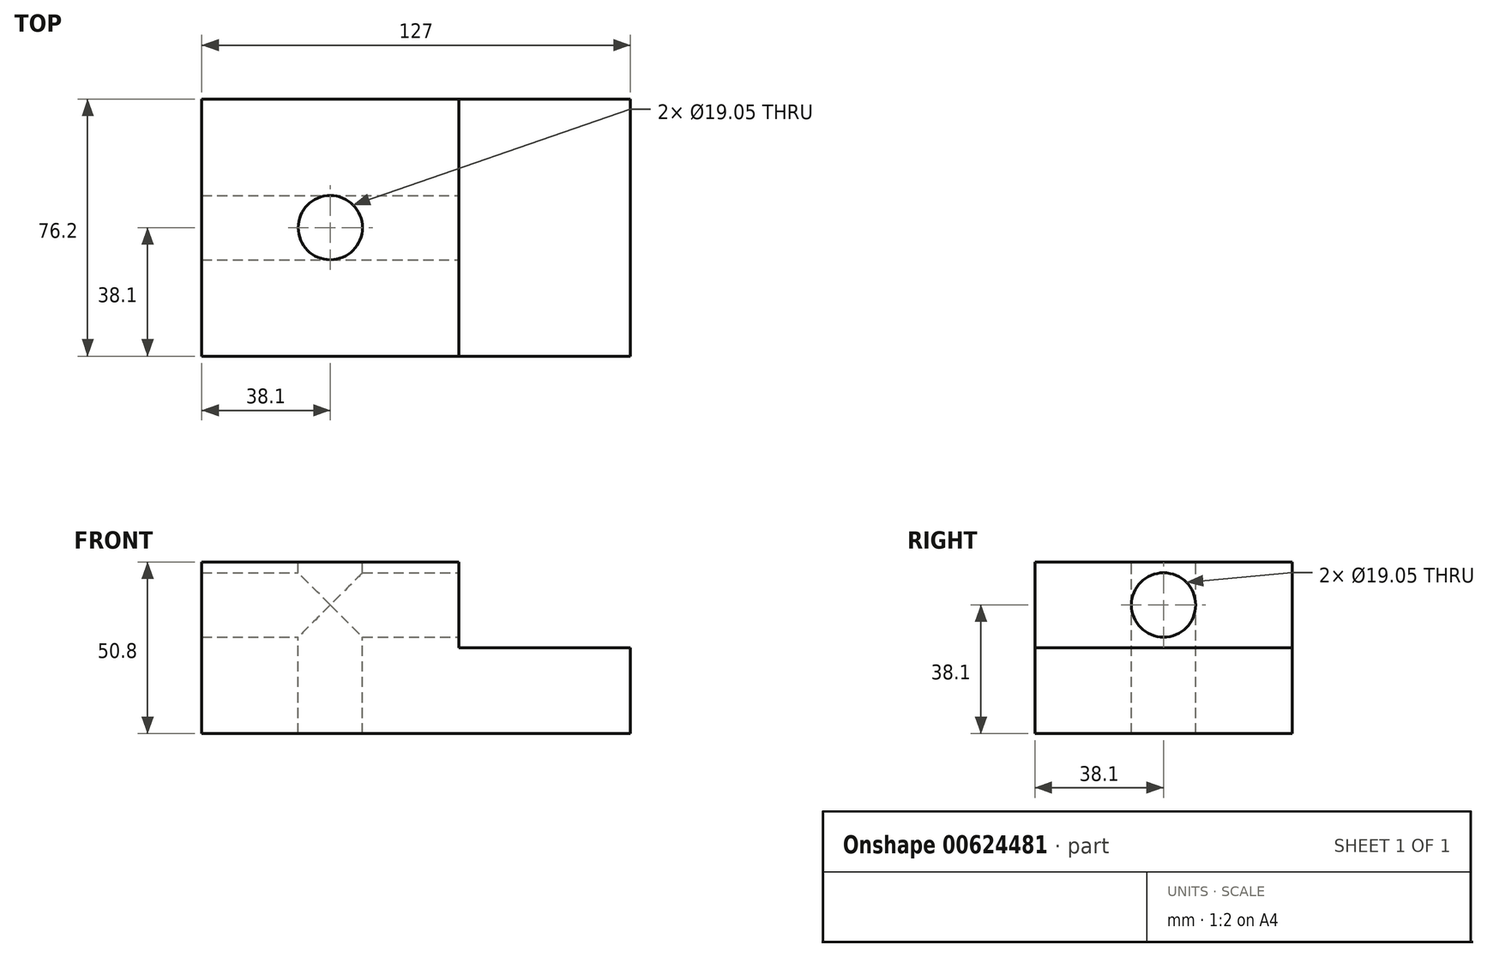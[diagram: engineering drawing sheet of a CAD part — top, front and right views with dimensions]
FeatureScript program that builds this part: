
annotation { "Feature Type Name" : "Feature", "Feature Type Description" : "" }
export const myFeature = defineFeature(function(context is Context, id is Id, definition is map)
    precondition{}
    {
        {
            var Q0;
            Q0=qCreatedBy(makeId("Front.planeOp"),FACE);
            var sketch = newSketch(context, id + "F0", { "sketchPlane" : qUnion([Q0])});
            skLineSegment(sketch, "E0.bottom", {"start": v(0, 0) * mm, "end": v(127, 0) * mm});
            skLineSegment(sketch, "E0.top", {"start": v(0, 50.8) * mm, "end": v(76.2, 50.8) * mm});
            skLineSegment(sketch, "E0.left", {"start": v(0, 0) * mm, "end": v(0, 50.8) * mm});
            skLineSegment(sketch, "E0.right", {"start": v(127, 0) * mm, "end": v(127, 25.4) * mm});
            skLineSegment(sketch, "E1.top", {"start": v(127, 25.4) * mm, "end": v(76.2, 25.4) * mm});
            skLineSegment(sketch, "E1.right", {"start": v(76.2, 50.8) * mm, "end": v(76.2, 25.4) * mm});
            skSolve(sketch);
        }
        {
            var Q0;
            Q0=makeQuery(id+"F0.imprint","IMPRINT",FACE,{"disambiguationData":[TD([[makeQuery(id+"F0.imprint","IMPRINT",EDGE,{"derivedFrom":sQuery(id+"F0.wireOp",EDGE,"E0.bottom")}),1.0]])]});
            extrude(context, id + "F1", {"entities" : qUnion([Q0]), "endBound" : BoundingType.SYMMETRIC, "depth" : 76.2 * mm, "offsetDistance" : 25.4 * mm});
        }
        {
            var Q0;
            Q0=makeQuery(id+"F1.opExtrude","SWEPT_FACE",FACE,{"disambiguationData":[OSD([sQuery(id+"F0.wireOp",EDGE,"E0.top")])]});
            var sketch = newSketch(context, id + "F2", { "sketchPlane" : qUnion([Q0])});
            skPoint(sketch, "E2", {"position": v(38.1, -38.1) * mm});
            skPoint(sketch, "E3", {"position": v(38.1, 0) * mm});
            skSolve(sketch);
        }
        {
            var Q0;
            Q0=sQuery(id+"F2.wireOp",VERTEX,"E3");
            var Q1;
            Q1=makeQuery(id+"F1.opExtrude","SWEPT_BODY",BODY,{"disambiguationData":[OSD([sQuery(id+"F0.wireOp",EDGE,"E0.bottom"),sQuery(id+"F0.wireOp",EDGE,"E0.top"),sQuery(id+"F0.wireOp",EDGE,"E0.left"),sQuery(id+"F0.wireOp",EDGE,"E0.right"),sQuery(id+"F0.wireOp",EDGE,"E1.top"),sQuery(id+"F0.wireOp",EDGE,"E1.right")])]});
            hole(context, id + "F3", {"style" : HoleStyle.SIMPLE, "endStyle" : HoleEndStyle.THROUGH, "holeDiameter" : 19.05 * mm, "majorDiameter" : 6.35 * mm, "isTappedThrough" : true, "tappedDepth" : 12.7 * mm, "tapClearance" : 3, "locations" : qUnion([Q0]), "scope" : qUnion([Q1])});
        }
        {
            var Q0;
            Q0=makeQuery(id+"F1.opExtrude","SWEPT_FACE",FACE,{"disambiguationData":[OSD([sQuery(id+"F0.wireOp",EDGE,"E1.right")])]});
            var sketch = newSketch(context, id + "F4", { "sketchPlane" : qUnion([Q0])});
            skPoint(sketch, "E4", {"position": v(0, 50.8) * mm});
            skPoint(sketch, "E5", {"position": v(-38.1, 38.1) * mm});
            skPoint(sketch, "E6", {"position": v(0, 38.1) * mm});
            skSolve(sketch);
        }
        {
            var Q0;
            Q0=sQuery(id+"F4.wireOp",VERTEX,"E6");
            var Q1;
            Q1=makeQuery(id+"F1.opExtrude","SWEPT_BODY",BODY,{"disambiguationData":[OSD([sQuery(id+"F0.wireOp",EDGE,"E0.bottom"),sQuery(id+"F0.wireOp",EDGE,"E0.top"),sQuery(id+"F0.wireOp",EDGE,"E0.left"),sQuery(id+"F0.wireOp",EDGE,"E0.right"),sQuery(id+"F0.wireOp",EDGE,"E1.top"),sQuery(id+"F0.wireOp",EDGE,"E1.right")])]});
            hole(context, id + "F5", {"style" : HoleStyle.SIMPLE, "endStyle" : HoleEndStyle.THROUGH, "holeDiameter" : 19.05 * mm, "majorDiameter" : 6.35 * mm, "isTappedThrough" : true, "tappedDepth" : 12.7 * mm, "tapClearance" : 3, "locations" : qUnion([Q0]), "scope" : qUnion([Q1])});
        }
    });
